# Revit family: URA_Eclairage_de_Securite_URALIFE V_NOIR_BAES – pose Murale
name_source: partatom
category: Luminaires
units: mm (PartAtom-declared; Revit-internal decimal feet)

## family parameters
Cote de connecteur circulaire = Utiliser le diamètre
Couper avec des vides une fois chargée = Non
Hôte = Face
Numéro OmniClass = 23.80.70.11.21
Partagée = Non
Repere pour localisation dans la piece = Non
Source d'éclairage = Non
Titre OmniClass = Emergency Lighting
Type d'élément = Normal

## types (19) — shared parameters
Alimentation de secours = Autonome (batterie individuelle)
Classe de protection = II
Conditions Générale d'Utilisation = https://export.legrand.com
Couleur = Noir
Elévation par défaut = 2300 mm
Fabricant = URA
Fréquence = 50-60
IK = 07
IP = 43
Matière = Plastique
Objet Connecté = Oui
Percement = 250 mm  [stored 0.82021 ft]
Puissance du système = 1 W
Système de contrôle = Surveillance centralisée
Temperature d'utilisation MIN-MAX = 0-35
Tension = 230 AC
Type de commutation = Non permanent
Type de connexion = autre
URL = www.ura.fr
Visibilité AMB Encastré horizontale = Non
Visibilité EVAC Saillie horizontale = Non
capacité des bornes = 1.5
source lumineuse = LED non interchangeable
zero-valued in all types: Entraxe de fixation verticale

## per-type parameters (varying)
| type | Autonomie | Batterie de rechange | Consommation en veille | Désignation produit | Entraxe de fixation horizontale | Flux lumineux utile | Fonction | Hauteur | Hauteur encastrement | Largeur | Largeur encastrement | Longueur | Longueur d'encastrement | Mode de pose | Picto AMB | Picto EVAC | Référence / Modèle | Type de pictogramme | Visibilité AMB Equerre | Visibilité AMB Saillie horizontale | Visibilité EVAC Equerre | Visibilité EVAC Saillie horizontale rect | Visibilité EVAC Saillie verticale | état des accus |
| 10-BAES Evacuation SATI Adressable pose murale en drapeau avec équerre (noir) | 1H | UR-111920 | 4.0 mA | BAES URALIFE V NOIR, EVACUATION, SATI ADRESSABLE, POSE PLAFOND ENCASTREE OU SAILLIE | 184-188 | 45 lm | Éclairage d'évacuation | 138 mm  [stored 0.452756 ft] | 55 mm  [stored 0.180446 ft] | 62 mm  [stored 0.203412 ft] | 70 mm  [stored 0.229659 ft] | 219 mm  [stored 0.718504 ft] | 245 mm  [stored 0.803806 ft] | En saillie et encastré | Non | Oui | UR-118419V | Feuillet/plaque inséré(e) | Non | Non | Oui | Non | Non | Lithium-ion |
| 15-BAES+BAEH SATI Adressable pose murale en drapeau avec équerre (noir) | 1H+5H | UR-111920 | 4.0 mA | BAES+BAEH URALIFE V NOIR, SATI ADRESSABLE, POSE PLAFOND ENCASTREE OU SAILLIE | 184-188 | 45 lm | Éclairage d'évacuation et d'ambiance | 138 mm  [stored 0.452756 ft] | 55 mm  [stored 0.180446 ft] | 62 mm  [stored 0.203412 ft] | 70 mm  [stored 0.229659 ft] | 219 mm  [stored 0.718504 ft] | 245 mm  [stored 0.803806 ft] | En saillie et encastré | Non | Oui | UR-118449V | Feuillet/plaque inséré(e) | Non | Non | Oui | Non | Non | Lithium-ion |
| 18-BAES+DBR SATI Adressable pose murale en drapeau avec équerre (noir) | 1H | UR-111920 | 4.0 mA | BAES+DBR URALIFE V NOIR, SATI ADRESSABLE, POSE PLAFOND ENCASTREE OU SAILLIE | 184-188 | 45 lm | Éclairage d'évacuation | 138 mm  [stored 0.452756 ft] | 55 mm  [stored 0.180446 ft] | 62 mm  [stored 0.203412 ft] | 70 mm  [stored 0.229659 ft] | 219 mm  [stored 0.718504 ft] | 245 mm  [stored 0.803806 ft] | En saillie et encastré | Non | Oui | UR-118459V | Feuillet/plaque inséré(e) | Non | Non | Oui | Non | Non | Lithium-ion |
| 11-BAES Evacuation SATI Adressable pose murale verticale en saillie (noir) | 1H | UR-111920 | 4.0 mA | BAES URALIFE V NOIR, EVACUATION, SATI ADRESSABLE, POSE PLAFOND ENCASTREE OU SAILLIE | 184-188 | 45 lm | Éclairage d'évacuation | 138 mm  [stored 0.452756 ft] | 55 mm  [stored 0.180446 ft] | 62 mm  [stored 0.203412 ft] | 70 mm  [stored 0.229659 ft] | 219 mm  [stored 0.718504 ft] | 245 mm  [stored 0.803806 ft] | En saillie et encastré | Non | Oui | UR-118419V | Feuillet/plaque inséré(e) | Non | Non | Non | Non | Oui | Lithium-ion |
| 16-BAES+BAEH SATI Adressable pose murale verticale en saillie (noir) | 1H+5H | UR-111920 | 4.0 mA | BAES+BAEH URALIFE V NOIR, SATI ADRESSABLE, POSE PLAFOND ENCASTREE OU SAILLIE | 184-188 | 45 lm | Éclairage d'évacuation et d'ambiance | 138 mm  [stored 0.452756 ft] | 55 mm  [stored 0.180446 ft] | 62 mm  [stored 0.203412 ft] | 70 mm  [stored 0.229659 ft] | 219 mm  [stored 0.718504 ft] | 245 mm  [stored 0.803806 ft] | En saillie et encastré | Non | Oui | UR-118449V | Feuillet/plaque inséré(e) | Non | Non | Non | Non | Oui | Lithium-ion |
| 19-BAES+DBR SATI Adressable pose murale verticale en saillie (noir) | 1H | UR-111920 | 4.0 mA | BAES+DBR URALIFE V NOIR, SATI ADRESSABLE, POSE PLAFOND ENCASTREE OU SAILLIE | 184-188 | 45 lm | Éclairage d'évacuation | 138 mm  [stored 0.452756 ft] | 55 mm  [stored 0.180446 ft] | 62 mm  [stored 0.203412 ft] | 70 mm  [stored 0.229659 ft] | 219 mm  [stored 0.718504 ft] | 245 mm  [stored 0.803806 ft] | En saillie et encastré | Non | Oui | UR-118459V | Feuillet/plaque inséré(e) | Non | Non | Non | Non | Oui | Lithium-ion |
| 13-BAES Ambiance SATI Adressable pose murale en drapeau avec equerre (noir) | 1H | UR-111921 | 3.5 mA | BAES URALIFE V NOIR, AMBIANCE, SATI ADRESSABLE, POSE PLAFOND ENCASTREE OU SAILLIE | 184-188 | 400 lm | Éclairage d'ambiance (anti-panique) | 36 mm  [stored 0.11811 ft] | 55 mm  [stored 0.180446 ft] | 62 mm  [stored 0.203412 ft] | 70 mm  [stored 0.229659 ft] | 219 mm  [stored 0.718504 ft] | 245 mm  [stored 0.803806 ft] | En saillie et encastré | Oui | Non | UR-118429V |  | Oui | Non | Non | Non | Non | NiMh |
| 12-BAES Ambiance SATI Adressable pose murale en saillie (noir) | 1H | UR-111921 | 3.5 mA | BAES URALIFE V NOIR, AMBIANCE, SATI ADRESSABLE, POSE PLAFOND ENCASTREE OU SAILLIE | 184-188 | 400 lm | Éclairage d'ambiance (anti-panique) | 36 mm  [stored 0.11811 ft] | 55 mm  [stored 0.180446 ft] | 62 mm  [stored 0.203412 ft] | 70 mm  [stored 0.229659 ft] | 219 mm  [stored 0.718504 ft] | 245 mm  [stored 0.803806 ft] | En saillie et encastré | Oui | Non | UR-118429V |  | Non | Oui | Non | Non | Non | NiMh |
| .9-BAES Evacuation SATI Adressable pose murale en applique (noir) | 1H | UR-111920 | 4.0 mA | BAES URALIFE V NOIR, EVACUATION, SATI ADRESSABLE, POSE MURALE SAILLIE | 90-100 | 45 lm | Éclairage d'évacuation | 38 mm  [stored 0.124672 ft] | 0 mm  [stored 0 ft] | 106 mm  [stored 0.347769 ft] | 0 mm  [stored 0 ft] | 206 mm  [stored 0.675853 ft] | 0 mm  [stored 0 ft] | Montage en saillie (mur) | Non | Oui | UR-118319V | Feuillet/plaque inséré(e) | Non | Non | Non | Oui | Non | Lithium-ion |
| 14-BAES+BAEH SATI Adressable pose murale en applique (noir) | 1H+5H | UR-111920 | 4.0 mA | BAES+BAEH, URALIFE V NOIR, SATI ADRESSABLE, POSE MURALE SAILLIE | 90-100 | 45 lm | Éclairage d'évacuation et d'ambiance | 38 mm  [stored 0.124672 ft] | 0 mm  [stored 0 ft] | 106 mm  [stored 0.347769 ft] | 0 mm  [stored 0 ft] | 206 mm  [stored 0.675853 ft] | 0 mm  [stored 0 ft] | Montage en saillie (mur) | Non | Oui | UR-118349V | Feuillet/plaque inséré(e) | Non | Non | Non | Oui | Non | Lithium-ion |
| 17-BAES+DBR SATI Adressable pose murale en applique (noir) | 1H | UR-111920 | 4.0 mA | BAES+DBR URALIFE V NOIR, SATI ADRESSABLE, POSE MURALE SAILLIE | 90-100 | 45 lm | Éclairage d'évacuation | 38 mm  [stored 0.124672 ft] | 0 mm  [stored 0 ft] | 106 mm  [stored 0.347769 ft] | 0 mm  [stored 0 ft] | 206 mm  [stored 0.675853 ft] | 0 mm  [stored 0 ft] | Montage en saillie (mur) | Non | Oui | UR-118359V | Feuillet/plaque inséré(e) | Non | Non | Non | Oui | Non | Lithium-ion |
| .1-BAES Evacuation SATI Connecté pose murale en applique (noir) | 1H | UR-111920 | 4.0 mA | BAES URALIFE V NOIR, EVACUATION, SATI CONNECTE, POSE MURALE SAILLIE | 90-100 | 45 lm | Éclairage d'évacuation | 38 mm  [stored 0.124672 ft] | 0 mm  [stored 0 ft] | 106 mm  [stored 0.347769 ft] | 0 mm  [stored 0 ft] | 206 mm  [stored 0.675853 ft] | 0 mm  [stored 0 ft] | Montage en saillie (mur) | Non | Oui | UR-118318V | Feuillet/plaque inséré(e) | Non | Non | Non | Oui | Non | Lithium-ion |
| .2-BAES Evacuation SATI Connecté pose murale en drapeau avec équerre (noir) | 1H | UR-111920 | 4.0 mA | BAES URALIFE V NOIR, EVACUATION, SATI CONNECTE, POSE PLAFOND ENCASTREE OU SAILLIE | 184-188 | 45 lm | Éclairage d'évacuation | 138 mm  [stored 0.452756 ft] | 55 mm  [stored 0.180446 ft] | 62 mm  [stored 0.203412 ft] | 70 mm  [stored 0.229659 ft] | 219 mm  [stored 0.718504 ft] | 245 mm  [stored 0.803806 ft] | En saillie et encastré | Non | Oui | UR-118418V | Feuillet/plaque inséré(e) | Non | Non | Oui | Non | Non | Lithium-ion |
| .3-BAES Evacuation SATI Connecté pose murale verticale en saillie (noir) | 1H | UR-111920 | 4.0 mA | BAES URALIFE V NOIR, EVACUATION, SATI CONNECTE, POSE PLAFOND ENCASTREE OU SAILLIE | 184-188 | 45 lm | Éclairage d'évacuation | 138 mm  [stored 0.452756 ft] | 55 mm  [stored 0.180446 ft] | 62 mm  [stored 0.203412 ft] | 70 mm  [stored 0.229659 ft] | 219 mm  [stored 0.718504 ft] | 245 mm  [stored 0.803806 ft] | En saillie et encastré | Non | Oui | UR-118418V | Feuillet/plaque inséré(e) | Non | Non | Non | Non | Oui | Lithium-ion |
| .6-BAES+BAEH SATI Connecté pose murale en applique (noir) | 1H+5H | UR-111920 | 4.0 mA | BAES+BAEH URALIFE V NOIR, SATI CONNECTE, POSE MURALE SAILLIE | 90-100 | 45 lm | Éclairage d'évacuation et d'ambiance | 38 mm  [stored 0.124672 ft] | 0 mm  [stored 0 ft] | 106 mm  [stored 0.347769 ft] | 0 mm  [stored 0 ft] | 206 mm  [stored 0.675853 ft] | 0 mm  [stored 0 ft] | Montage en saillie (mur) | Non | Oui | UR-118348V | Feuillet/plaque inséré(e) | Non | Non | Non | Oui | Non | Lithium-ion |
| .7-BAES+BAEH SATI Connecté pose murale en drapeau avec équerre (noir) | 1H+5H | UR-111920 | 4.0 mA | BAES+BAEH URALIFE V NOIR, SATI CONNECTE, POSE PLAFOND ENCASTREE OU SAILLIE | 184-188 | 45 lm | Éclairage d'évacuation et d'ambiance | 138 mm  [stored 0.452756 ft] | 55 mm  [stored 0.180446 ft] | 62 mm  [stored 0.203412 ft] | 70 mm  [stored 0.229659 ft] | 219 mm  [stored 0.718504 ft] | 245 mm  [stored 0.803806 ft] | En saillie et encastré | Non | Oui | UR-118448V | Feuillet/plaque inséré(e) | Non | Non | Oui | Non | Non | Lithium-ion |
| .8-BAES+BAEH SATI Connecté pose murale verticale en saillie (noir) | 1H+5H | UR-111920 | 4.0 mA | BAES+BAEH URALIFE V NOIR, SATI CONNECTE, POSE PLAFOND ENCASTREE OU SAILLIE | 184-188 | 45 lm | Éclairage d'évacuation et d'ambiance | 138 mm  [stored 0.452756 ft] | 55 mm  [stored 0.180446 ft] | 62 mm  [stored 0.203412 ft] | 70 mm  [stored 0.229659 ft] | 219 mm  [stored 0.718504 ft] | 245 mm  [stored 0.803806 ft] | En saillie et encastré | Non | Oui | UR-118448V | Feuillet/plaque inséré(e) | Non | Non | Non | Non | Oui | Lithium-ion |
| .4-BAES Ambiance SATI Connecté pose murale en saillie (noir) | 1H | UR-111921 | 3.5 mA | BAES URALIFE V NOIR, AMBIANCE, SATI CONNECTE, POSE PLAFOND ENCASTREE OU SAILLIE | 184-188 | 400 lm | Éclairage d'ambiance (anti-panique) | 36 mm  [stored 0.11811 ft] | 55 mm  [stored 0.180446 ft] | 62 mm  [stored 0.203412 ft] | 70 mm  [stored 0.229659 ft] | 219 mm  [stored 0.718504 ft] | 245 mm  [stored 0.803806 ft] | En saillie et encastré | Oui | Non | UR-118428V |  | Non | Oui | Non | Non | Non | NiMh |
| .5-BAES Ambiance SATI Connecté pose murale en drapeau avec equerre (noir) | 1H | UR-111921 | 3.5 mA | BAES URALIFE V NOIR, AMBIANCE, SATI CONNECTE, POSE PLAFOND ENCASTREE OU SAILLIE | 184-188 | 400 lm | Éclairage d'ambiance (anti-panique) | 36 mm  [stored 0.11811 ft] | 55 mm  [stored 0.180446 ft] | 62 mm  [stored 0.203412 ft] | 70 mm  [stored 0.229659 ft] | 219 mm  [stored 0.718504 ft] | 245 mm  [stored 0.803806 ft] | En saillie et encastré | Oui | Non | UR-118428V |  | Oui | Non | Non | Non | Non | NiMh |

note: [stored X ft] marks values corroborated as IEEE doubles in the binary element streams (Revit-internal decimal feet)
